# Revit family: Door_Single
name_source: partatom
category: Doors
units: mm (PartAtom-declared; Revit-internal decimal feet)

## family parameters
Always vertical = Yes
Cut with Voids When Loaded = No
Host = Wall
OmniClass Number = 23.30.10.00
OmniClass Title = Doors
Room Calculation Point = No
Shared = No

## types (1)
- Door_Single
    Analytic Construction = <None>
    COBie.Type = Yes
    COBie.Type.Area = 0 m²
    COBie.Type.Length = 0 mm  [stored 0 ft]
    COBie.Type.NominalHeight = 0 mm  [stored 0 ft]
    COBie.Type.NominalLength = 0 mm  [stored 0 ft]
    COBie.Type.NominalWidth = 0 mm  [stored 0 ft]
    COBie.Type.ReplacementCost = 0 $
    Construction Type = Steel
    Define Thermal Properties by = Schematic Type
    Door Opening Angle Limit = 120.00°
    Function = Interior
    Height = 2000 mm  [stored 6.56168 ft]
    Max Door Height = 2700 mm  [stored 8.85827 ft]
    Max Door Width = 950 mm  [stored 3.1168 ft]
    Min Door Height = 350 mm
    Min Door Width = 450 mm
    Pivot Plane 1 = 9.95 mm
    Pivot Plane 2 = 17.8 mm
    Show Lock = Yes
    Thickness = 43 mm  [stored 0.141076 ft]
    Wall Closure = By host
    Width = 1000 mm  [stored 3.28084 ft]

note: [stored X ft] marks values corroborated as IEEE doubles in the binary element streams (Revit-internal decimal feet)

## geometry (parser evidence)
native form markers: Sweep x15
no freeform markers — native parametric forms only
